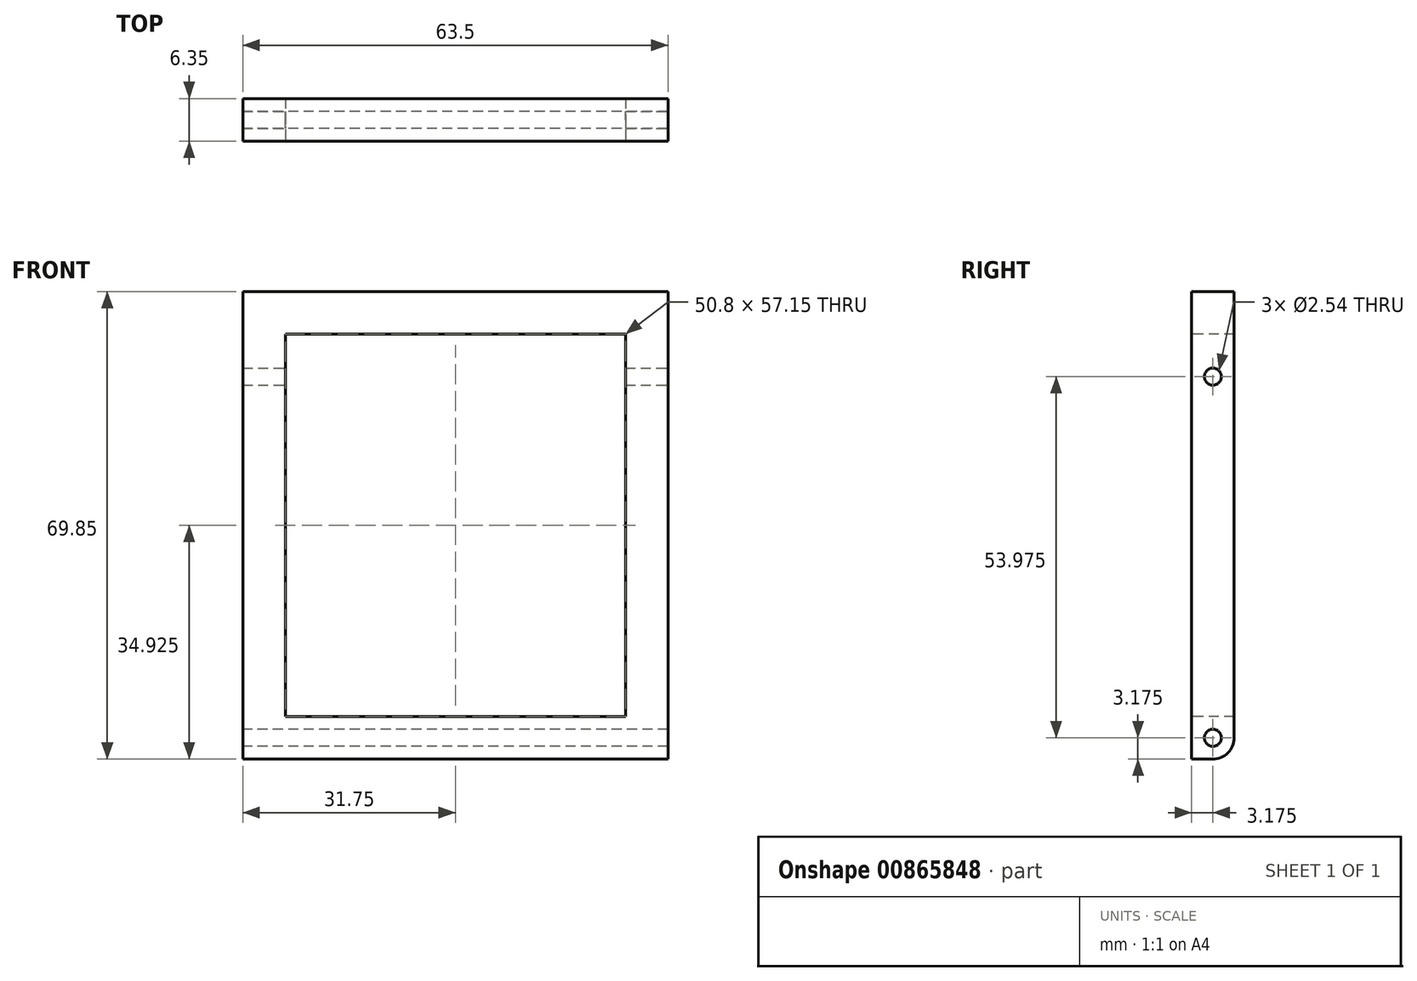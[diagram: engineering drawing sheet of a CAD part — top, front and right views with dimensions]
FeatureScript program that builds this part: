
annotation { "Feature Type Name" : "Feature", "Feature Type Description" : "" }
export const myFeature = defineFeature(function(context is Context, id is Id, definition is map)
    precondition{}
    {
        {
            var Q0;
            Q0=qCreatedBy(makeId("Front.planeOp"),FACE);
            var sketch = newSketch(context, id + "F0", { "sketchPlane" : qUnion([Q0])});
            skLineSegment(sketch, "E0.bottom", {"start": v(0, 0) * mm, "end": v(63.5, 0) * mm});
            skLineSegment(sketch, "E0.top", {"start": v(0, -69.85) * mm, "end": v(63.5, -69.85) * mm});
            skLineSegment(sketch, "E0.left", {"start": v(0, 0) * mm, "end": v(0, -69.85) * mm});
            skLineSegment(sketch, "E0.right", {"start": v(63.5, 0) * mm, "end": v(63.5, -69.85) * mm});
            skLineSegment(sketch, "E1.0", {"start": v(6.35, -6.35) * mm, "end": v(57.15, -6.35) * mm});
            skLineSegment(sketch, "E1.1", {"start": v(6.35, -6.35) * mm, "end": v(6.35, -63.5) * mm});
            skLineSegment(sketch, "E1.2", {"start": v(6.35, -63.5) * mm, "end": v(57.15, -63.5) * mm});
            skLineSegment(sketch, "E1.3", {"start": v(57.15, -6.35) * mm, "end": v(57.15, -63.5) * mm});
            skSolve(sketch);
        }
        {
            var Q0;
            Q0=makeQuery(id+"F0.imprint","IMPRINT",FACE,{"disambiguationData":[TD([[makeQuery(id+"F0.imprint","IMPRINT",EDGE,{"derivedFrom":sQuery(id+"F0.wireOp",EDGE,"E0.bottom")}),-1.0]])]});
            extrude(context, id + "F1", {"entities" : qUnion([Q0]), "oppositeDirection" : true, "depth" : 6.35 * mm, "offsetDistance" : 25.4 * mm});
        }
        {
            var Q0;
            Q0=makeQuery(id+"F1.opExtrude","SWEPT_FACE",FACE,{"disambiguationData":[OSD([sQuery(id+"F0.wireOp",EDGE,"E0.left")])]});
            var sketch = newSketch(context, id + "F2", { "sketchPlane" : qUnion([Q0])});
            skCircle(sketch, "E2", {"center": v(-3.18, -66.67) * mm, "radius": 1.27 * mm});
            skPoint(sketch, "E2.centerSnap0", {"position": v(-3.18, -69.85) * mm});
            skSolve(sketch);
        }
        {
            var Q0;
            Q0 = qSketchRegion(id + "F2", true);
            extrude(context, id + "F3", {"entities" : qUnion([Q0]), "operationType" : NewBodyOperationType.REMOVE, "endBound" : BoundingType.THROUGH_ALL, "oppositeDirection" : true, "depth" : 25.4 * mm, "offsetDistance" : 25.4 * mm});
        }
        {
            var Q0;
            Q0=makeQuery(id+"F1.opExtrude","CAP_EDGE",EDGE,{"disambiguationData":[OSD([sQuery(id+"F0.wireOp",EDGE,"E0.top")])],"isStart":false});
            fillet(context, id + "F4", {"entities" : qUnion([Q0]), "radius" : 3.17 * mm, "tangentPropagation" : true, "allowEdgeOverflow" : false});
        }
        {
            var Q0;
            Q0=makeQuery(id+"F1.opExtrude","SWEPT_FACE",FACE,{"disambiguationData":[OSD([sQuery(id+"F0.wireOp",EDGE,"E0.right")])]});
            var sketch = newSketch(context, id + "F5", { "sketchPlane" : qUnion([Q0])});
            skLineSegment(sketch, "E3", {"start": v(0, -12.7) * mm, "end": v(6.35, -12.7) * mm, "construction": true});
            skCircle(sketch, "E4", {"center": v(3.18, -12.7) * mm, "radius": 1.27 * mm});
            skSolve(sketch);
        }
        {
            var Q0;
            Q0 = qSketchRegion(id + "F5", true);
            extrude(context, id + "F6", {"entities" : qUnion([Q0]), "operationType" : NewBodyOperationType.REMOVE, "endBound" : BoundingType.THROUGH_ALL, "oppositeDirection" : true, "depth" : 25.4 * mm, "offsetDistance" : 25.4 * mm});
        }
    });
